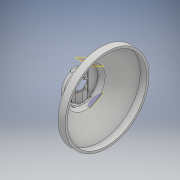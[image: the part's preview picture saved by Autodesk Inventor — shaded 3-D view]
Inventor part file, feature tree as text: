
AUTODESK INVENTOR PART (.ipt)
format: ipt  version: 2018 (Build 220112000, 112)  size: 2,480,128 bytes
history: native  units: mm
features: sketch x66, extrude x59, fillet x23, revolve x2, plane x2, mirror x1
ambient origin geometry x8: Origin, YZ Plane, XZ Plane, XY Plane, X Axis, Y Axis, Z Axis, Center Point
bodies: Solid1 (feature_tree)
feature tree (153):
  extrude  "Extrusion1"  TaperAngle=0.0deg  [1 undecoded]
  extrude  "Extrusion2"  Depth=10.0mm TaperAngle=0.0deg
  extrude  "Extrusion3"  Depth=50.0mm
  extrude  "Extrusion4"  TaperAngle=0.0deg  [1 undecoded]
  extrude  "Extrusion5"  Depth=10.0mm TaperAngle=0.0deg
  sketch  "Sketch6"  dims[d19=10.0mm d20=0.0mm d21=40.0mm]
  extrude  "Extrusion6"  Depth=40.0mm
  extrude  "Extrusion7"  Depth=11.0mm TaperAngle=0.0deg
  extrude  "Extrusion8"  Depth=32.0mm TaperAngle=0.0deg
  extrude  "Extrusion9"  Depth=32.0mm TaperAngle=0.0deg
  extrude  "Extrusion10"  Depth=10.0mm TaperAngle=0.0deg
  extrude  "Extrusion11"  Depth=10.0mm TaperAngle=0.0deg
  extrude  "Extrusion12"  TaperAngle=0.0deg  [1 undecoded]
  extrude  "Extrusion14"  Depth=48.3mm
  extrude  "Extrusion15"  TaperAngle=0.0deg  [1 undecoded]
  extrude  "Extrusion16"  Depth=10.0mm TaperAngle=0.0deg
  extrude  "Extrusion17"  Depth=11.63mm TaperAngle=0.0deg
  sketch  "Sketch21"  dims[d83=0.0mm d84=0.0mm d85=0.0mm d86=0.0mm]
  extrude  "Extrusion19"  Depth=11.63mm TaperAngle=0.0deg
  extrude  "Extrusion20"  TaperAngle=0.0deg  [1 undecoded]
  extrude  "Extrusion21"  Depth=10.0mm TaperAngle=0.0deg
  extrude  "Extrusion22"  TaperAngle=0.0deg  [1 undecoded]
  extrude  "Extrusion23"  Depth=2.86mm TaperAngle=0.0deg
  extrude  "Extrusion24"  Depth=2.01mm
  extrude  "Extrusion25"  Depth=10.0mm TaperAngle=0.0deg
  sketch  "Sketch33"  dims[d115=7.8mm d116=0.0mm d117=0.0mm d118=0.0mm]
  extrude  "Extrusion26"  Depth=7.8mm TaperAngle=0.0deg
  extrude  "Extrusion27"  TaperAngle=0.0deg  [1 undecoded]
  extrude  "Extrusion28"  Depth=22.0mm TaperAngle=0.0deg
  extrude  "Extrusion29"  Depth=17.0mm TaperAngle=0.0deg
  extrude  "Extrusion30"  Depth=2.0mm
  extrude  "Extrusion31"  Depth=6.95mm TaperAngle=0.0deg
  extrude  "Extrusion32"  Depth=18.0mm TaperAngle=0.0deg
  extrude  "Extrusion33"  Depth=1.02mm
  sketch  "Sketch42"  dims[d151=2.0mm d152=2.0mm]
  extrude  "Extrusion34"  Depth=7.72mm TaperAngle=0.0deg
  extrude  "Extrusion36"  Depth=2.0mm
  extrude  "Extrusion37"  Depth=2.0mm
  revolve  "Revolution3"  [1 undecoded]
  extrude  "Extrusion38"  Depth=2.0mm
  extrude  "Extrusion39"  Depth=10.0mm TaperAngle=0.0deg
  fillet  "Fillet1"  Radius=7.83mm
  fillet  "Fillet2"  Radius=20.0mm
  sketch  "Sketch51"  dims[d171=2.0mm d172=2.0mm]
  extrude  "Extrusion41"  Depth=6.4mm TaperAngle=0.0deg
  mirror  "Mirror1"
  extrude  "Extrusion42"  Depth=2.0mm
  sketch  "Sketch54"  dims[d181=2.0mm d182=2.0mm]
  sketch  "Sketch55"  dims[d183=2.0mm d184=2.0mm]
  sketch  "Sketch56"  dims[d185=2.0mm]
  extrude  "Extrusion44"  Depth=2.0mm
  extrude  "Extrusion45"  Depth=2.0mm
  extrude  "Extrusion46"  TaperAngle=90.0deg  [1 undecoded]
  extrude  "Extrusion47"  Depth=2.0mm
  plane  "Work Plane2"
  extrude  "Extrusion48"  Depth=2.0mm
  extrude  "Extrusion49"  [1 undecoded]
  plane  "Work Plane5"
  extrude  "Extrusion50"  [1 undecoded]
  extrude  "Extrusion51"  [1 undecoded]
  fillet  "Fillet3"  [1 undecoded]
  fillet  "Fillet4"  [1 undecoded]
  extrude  "Extrusion52"  [1 undecoded]
  extrude  "Extrusion53"  [1 undecoded]
  extrude  "Extrusion54"  [1 undecoded]
  extrude  "Extrusion55"  [1 undecoded]
  fillet  "Fillet5"  [1 undecoded]
  extrude  "Extrusion57"  [1 undecoded]
  extrude  "Extrusion58"  [1 undecoded]
  extrude  "Extrusion59"  [1 undecoded]
  fillet  "Fillet7"  [1 undecoded]
  fillet  "Fillet8"  [1 undecoded]
  fillet  "Fillet9"  [1 undecoded]
  fillet  "Fillet10"  [1 undecoded]
  fillet  "Fillet11"  [1 undecoded]
  fillet  "Fillet12"  [1 undecoded]
  fillet  "Fillet13"  [1 undecoded]
  fillet  "Fillet14"  [1 undecoded]
  extrude  "Extrusion60"  [1 undecoded]
  extrude  "Extrusion61"  [1 undecoded]
  extrude  "Extrusion62"  [1 undecoded]
  extrude  "Extrusion63"  [1 undecoded]
  extrude  "Extrusion64"  [1 undecoded]
  extrude  "Extrusion65"  [1 undecoded]
  fillet  "Fillet15"  [1 undecoded]
  fillet  "Fillet16"  [1 undecoded]
  fillet  "Fillet17"  [1 undecoded]
  fillet  "Fillet18"  [1 undecoded]
  fillet  "Fillet19"  [1 undecoded]
  revolve  "Revolution4"  [1 undecoded]
  fillet  "Fillet20"  [1 undecoded]
  fillet  "Fillet21"  [1 undecoded]
  fillet  "Fillet22"  [1 undecoded]
  fillet  "Fillet23"  [1 undecoded]
  fillet  "Fillet24"  [1 undecoded]
  sketch  "Sketch1"  dims[d0=10.0mm d1=0.0mm d2=0.0mm d3=0.0mm]
  sketch  "Sketch2"  dims[d4=0.0mm d5=0.0mm d6=10.0mm d7=0.0mm]
  sketch  "Sketch3"  dims[d8=10.0mm d9=0.0mm d10=50.0mm]
  sketch  "Sketch4"  dims[d11=10.0mm d12=0.0mm d13=0.0mm d14=0.0mm]
  sketch  "Sketch5"  dims[d15=0.0mm d16=0.0mm d17=10.0mm d18=0.0mm]
  sketch  "Sketch7"  dims[d22=38.0mm d23=11.0mm d24=0.0mm]
  sketch  "Sketch8"  dims[d25=9.5mm d26=0.0mm d33=32.0mm d34=0.0mm]
  sketch  "Sketch9"  dims[d37=32.0mm d38=0.0mm d39=32.0mm d40=0.0mm]
  sketch  "Sketch10"  dims[d41=32.0mm d42=0.0mm d45=10.0mm d46=0.0mm]
  sketch  "Sketch11"  dims[d47=10.0mm d48=0.0mm d49=10.0mm d50=0.0mm]
  sketch  "Sketch12"  dims[d51=0.0mm d52=0.0mm d53=0.0mm d54=0.0mm]
  sketch  "Sketch13"  dims[d65=46.0mm d66=48.3mm]
  sketch  "Sketch16"  dims[d67=9.0mm d68=0.0mm d69=0.0mm d70=0.0mm]
  sketch  "Sketch18"  dims[d71=0.0mm d72=0.0mm d73=10.0mm d74=0.0mm]
  sketch  "Sketch19"  dims[d75=5.0mm d76=0.0mm d77=11.63mm d78=0.0mm]
  sketch  "Sketch20"  dims[d79=11.63mm d80=0.0mm d81=11.63mm d82=0.0mm]
  sketch  "Sketch22"  dims[d87=30.0mm d88=10.0mm d89=0.0mm]
  sketch  "Sketch23"  dims[d92=10.0mm d93=0.0mm d94=0.0mm d95=0.0mm]
  sketch  "Sketch24"  dims[d96=135.0deg d99=2.86mm d100=0.0mm]
  sketch  "Sketch25"  dims[d101=0.0mm d102=0.0mm d105=2.01mm]
  sketch  "Sketch31"  dims[d106=2.22mm d107=10.0mm d108=0.0mm]
  sketch  "Sketch32"  dims[d109=10.0mm d110=0.0mm d113=7.8mm d114=0.0mm]
  sketch  "Sketch34"  dims[d119=16.0mm d120=0.0mm d121=22.0mm d122=0.0mm]
  sketch  "Sketch35"  dims[d123=22.0mm d124=0.0mm d126=17.0mm d127=0.0mm]
  sketch  "Sketch36"  dims[d128=17.0mm d129=0.0mm d130=2.0mm]
  sketch  "Sketch37"  dims[d131=2.0mm d132=6.95mm d133=0.0mm]
  sketch  "Sketch38"  dims[d134=6.95mm d135=0.0mm d136=18.0mm d137=0.0mm]
  sketch  "Sketch39"  dims[d138=16.0mm d139=0.0mm d140=1.02mm]
  sketch  "Sketch40"  dims[d143=15.5mm d144=0.0mm d146=7.72mm d147=0.0mm]
  sketch  "Sketch41"  dims[d148=17.0mm d149=0.0mm d150=2.0mm]
  sketch  "Sketch43"  dims[d153=2.0mm d154=2.0mm]
  sketch  "Sketch45"  dims[d155=2.0mm d156=2.0mm]
  sketch  "Sketch47"  dims[d157=2.0mm d158=10.0mm d159=0.0mm d160=7.83mm d161=0.0mm d162=20.0mm d163=0.0mm]
  sketch  "Sketch48"  dims[d164=0.0mm d165=0.0mm d166=6.4mm d167=0.0mm]
  sketch  "Sketch49"  dims[d168=6.14mm d169=0.0mm d170=2.0mm]
  sketch  "Sketch52"  dims[d173=2.0mm d174=2.0mm]
  sketch  "Sketch53"  dims[d175=1.5mm d176=1.5mm d177=3.0mm d178=10.0mm d180=90.0deg]
  sketch  "Sketch57"
  sketch  "Sketch60"
  sketch  "Sketch61"
  sketch  "Sketch62"
  sketch  "Sketch63"
  sketch  "Sketch65"
  sketch  "Sketch66"
  sketch  "Sketch67"
  sketch  "Sketch68"
  sketch  "Sketch69"
  sketch  "Sketch70"
  sketch  "Sketch72"
  sketch  "Sketch73"
  sketch  "Sketch74"
  sketch  "Sketch75"
  sketch  "Sketch76"
  sketch  "Sketch78"
  sketch  "Sketch80"
  sketch  "Sketch81"
  sketch  "Sketch82"
  sketch  "Sketch83"
note: 47 required parameter values undecoded (feature->parameter linkage not recoverable at this tier; creation-order binding heuristic only, values carry confidence <= 0.55)